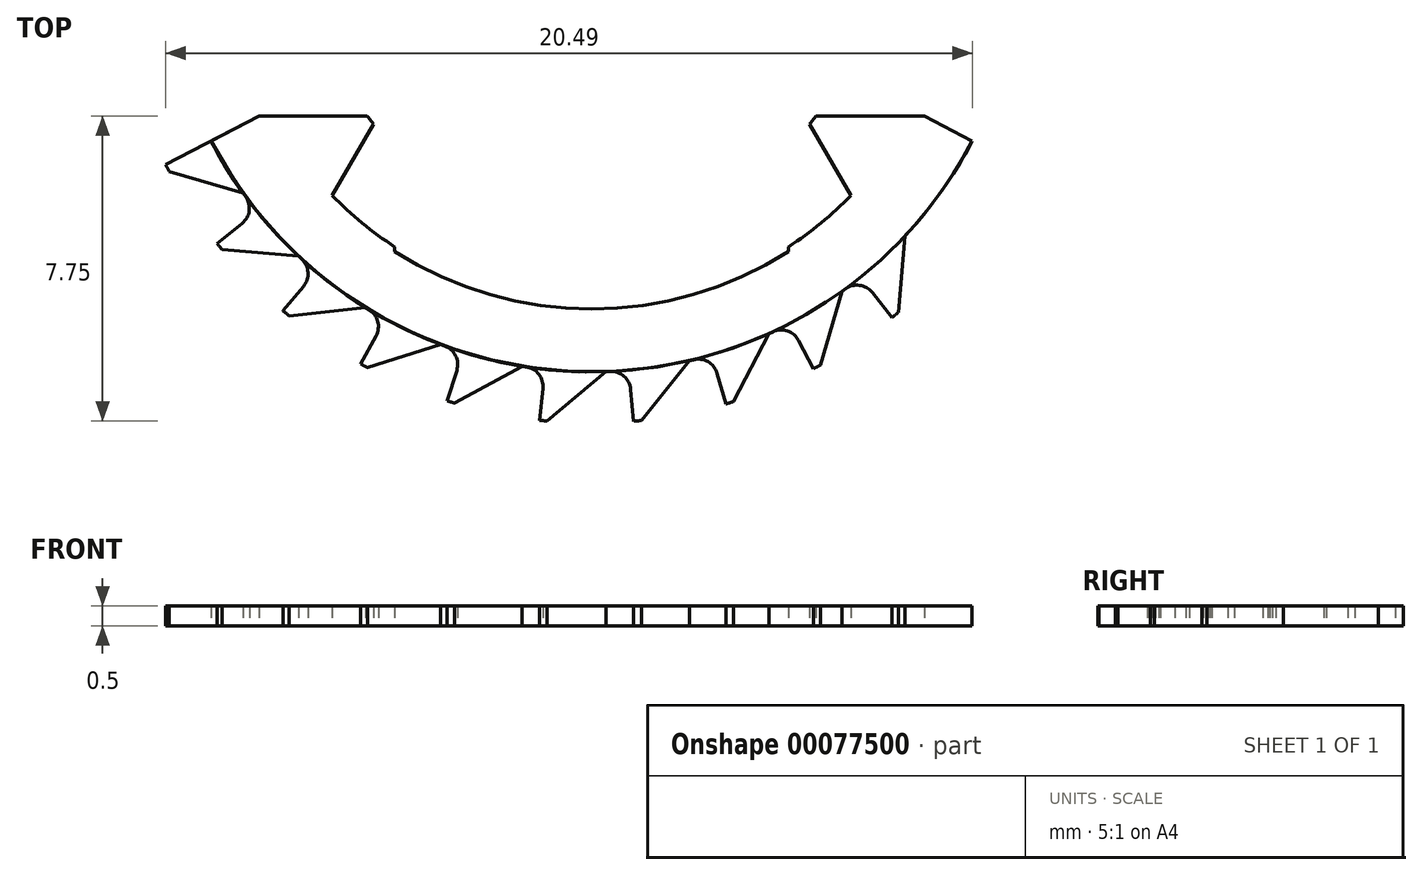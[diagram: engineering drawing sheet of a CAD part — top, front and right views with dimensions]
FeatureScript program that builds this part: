
annotation { "Feature Type Name" : "Feature", "Feature Type Description" : "" }
export const myFeature = defineFeature(function(context is Context, id is Id, definition is map)
    precondition{}
    {
        {
            var Q0;
            Q0=qCreatedBy(makeId("Top.planeOp"),FACE);
            var sketch = newSketch(context, id + "F0", { "sketchPlane" : qUnion([Q0])});
            skArc(sketch, "E0", {"start": v(5, -7.72) * mm, "mid": v(5.83, -7.12) * mm, "end": v(6.6, -6.42) * mm});
            skArc(sketch, "E1", {"start": v(-5, -7.84) * mm, "mid": v(0, -9.3) * mm, "end": v(5, -7.84) * mm});
            skArc(sketch, "E2", {"start": v(7.64, -9.51) * mm, "mid": v(7.71, -9.45) * mm, "end": v(7.8, -9.39) * mm});
            skCircle(sketch, "E3", {"center": v(0, 0) * mm, "radius": 10.9 * mm});
            skLineSegment(sketch, "E4", {"start": v(0, 0) * mm, "end": v(-10.82, -5.63) * mm});
            skLineSegment(sketch, "E5", {"start": v(0, 0) * mm, "end": v(9.67, -5.03) * mm});
            skLineSegment(sketch, "E6", {"start": v(0, 0) * mm, "end": v(7.64, -9.51) * mm, "construction": true});
            skLineSegment(sketch, "E7", {"start": v(6.82, -8.5) * mm, "end": v(7.64, -9.51) * mm});
            skLineSegment(sketch, "E8", {"start": v(7.8, -9.39) * mm, "end": v(7.96, -7.45) * mm});
            skLineSegment(sketch, "E9", {"start": v(0, 0) * mm, "end": v(9.35, -7.84) * mm, "construction": true});
            skLineSegment(sketch, "E10.1.0", {"start": v(5.8, -10.73) * mm, "end": v(6.36, -8.86) * mm});
            skArc(sketch, "E10.1.1", {"start": v(5.63, -10.82) * mm, "mid": v(5.72, -10.77) * mm, "end": v(5.8, -10.73) * mm});
            skLineSegment(sketch, "E10.1.2", {"start": v(5.03, -9.67) * mm, "end": v(5.63, -10.82) * mm});
            skLineSegment(sketch, "E10.2.0", {"start": v(3.6, -11.66) * mm, "end": v(4.5, -9.92) * mm});
            skArc(sketch, "E10.2.1", {"start": v(3.41, -11.71) * mm, "mid": v(3.5, -11.68) * mm, "end": v(3.6, -11.66) * mm});
            skLineSegment(sketch, "E10.2.2", {"start": v(3.05, -10.46) * mm, "end": v(3.41, -11.71) * mm});
            skLineSegment(sketch, "E10.3.0", {"start": v(1.26, -12.13) * mm, "end": v(2.48, -10.61) * mm});
            skArc(sketch, "E10.3.1", {"start": v(1.06, -12.15) * mm, "mid": v(1.16, -12.14) * mm, "end": v(1.26, -12.13) * mm});
            skLineSegment(sketch, "E10.3.2", {"start": v(0.95, -10.86) * mm, "end": v(1.06, -12.15) * mm});
            skLineSegment(sketch, "E10.4.0", {"start": v(-1.13, -12.15) * mm, "end": v(0.36, -10.9) * mm});
            skArc(sketch, "E10.4.1", {"start": v(-1.33, -12.13) * mm, "mid": v(-1.23, -12.14) * mm, "end": v(-1.13, -12.15) * mm});
            skLineSegment(sketch, "E10.4.2", {"start": v(-1.19, -10.84) * mm, "end": v(-1.33, -12.13) * mm});
            skLineSegment(sketch, "E10.5.0", {"start": v(-3.48, -11.7) * mm, "end": v(-1.77, -10.76) * mm});
            skArc(sketch, "E10.5.1", {"start": v(-3.67, -11.64) * mm, "mid": v(-3.57, -11.67) * mm, "end": v(-3.48, -11.7) * mm});
            skLineSegment(sketch, "E10.5.2", {"start": v(-3.28, -10.4) * mm, "end": v(-3.67, -11.64) * mm});
            skLineSegment(sketch, "E10.6.0", {"start": v(-5.7, -10.8) * mm, "end": v(-3.83, -10.2) * mm});
            skArc(sketch, "E10.6.1", {"start": v(-5.87, -10.7) * mm, "mid": v(-5.78, -10.74) * mm, "end": v(-5.7, -10.8) * mm});
            skLineSegment(sketch, "E10.6.2", {"start": v(-5.24, -9.56) * mm, "end": v(-5.87, -10.7) * mm});
            skLineSegment(sketch, "E10.7.0", {"start": v(-7.69, -9.47) * mm, "end": v(-5.75, -9.26) * mm});
            skArc(sketch, "E10.7.1", {"start": v(-7.84, -9.35) * mm, "mid": v(-7.77, -9.4) * mm, "end": v(-7.69, -9.47) * mm});
            skLineSegment(sketch, "E10.7.2", {"start": v(-7, -8.35) * mm, "end": v(-7.84, -9.35) * mm});
            skLineSegment(sketch, "E10.8.0", {"start": v(-9.39, -7.8) * mm, "end": v(-7.45, -7.96) * mm});
            skArc(sketch, "E10.8.1", {"start": v(-9.51, -7.64) * mm, "mid": v(-9.45, -7.71) * mm, "end": v(-9.39, -7.8) * mm});
            skLineSegment(sketch, "E10.8.2", {"start": v(-8.5, -6.82) * mm, "end": v(-9.51, -7.64) * mm});
            skLineSegment(sketch, "E10.9.0", {"start": v(-10.73, -5.8) * mm, "end": v(-8.86, -6.36) * mm});
            skArc(sketch, "E10.9.1", {"start": v(-10.82, -5.63) * mm, "mid": v(-10.77, -5.72) * mm, "end": v(-10.73, -5.8) * mm});
            skLineSegment(sketch, "E10.9.2", {"start": v(-9.67, -5.03) * mm, "end": v(-10.82, -5.63) * mm});
            skLineSegment(sketch, "E10.anchor1", {"start": v(0, 0) * mm, "end": v(7.8, -9.39) * mm, "construction": true});
            skLineSegment(sketch, "E10.anchor2", {"start": v(0, 0) * mm, "end": v(-9.58, -5.2) * mm, "construction": true});
            skArc(sketch, "E11", {"start": v(7.13, -8.88) * mm, "mid": v(6.8, -8.7) * mm, "end": v(6.44, -8.8) * mm});
            skArc(sketch, "E12.1.0", {"start": v(5.26, -10.1) * mm, "mid": v(4.98, -9.86) * mm, "end": v(4.6, -9.88) * mm});
            skArc(sketch, "E12.2.0", {"start": v(3.19, -10.93) * mm, "mid": v(2.96, -10.64) * mm, "end": v(2.59, -10.59) * mm});
            skArc(sketch, "E12.3.0", {"start": v(1, -11.35) * mm, "mid": v(0.82, -11.01) * mm, "end": v(0.47, -10.89) * mm});
            skArc(sketch, "E12.4.0", {"start": v(-1.24, -11.32) * mm, "mid": v(-1.34, -10.96) * mm, "end": v(-1.66, -10.77) * mm});
            skArc(sketch, "E12.5.0", {"start": v(-3.42, -10.86) * mm, "mid": v(-3.45, -10.5) * mm, "end": v(-3.73, -10.24) * mm});
            skArc(sketch, "E12.6.0", {"start": v(-5.48, -9.99) * mm, "mid": v(-5.43, -9.62) * mm, "end": v(-5.66, -9.32) * mm});
            skArc(sketch, "E12.7.0", {"start": v(-7.32, -8.72) * mm, "mid": v(-7.2, -8.37) * mm, "end": v(-7.37, -8.03) * mm});
            skArc(sketch, "E12.8.0", {"start": v(-8.88, -7.13) * mm, "mid": v(-8.7, -6.8) * mm, "end": v(-8.8, -6.44) * mm});
            skLineSegment(sketch, "E12.anchor1", {"start": v(6.44, -8.8) * mm, "end": v(0, 0) * mm, "construction": true});
            skLineSegment(sketch, "E12.anchor2", {"start": v(0, 0) * mm, "end": v(-8.8, -6.44) * mm, "construction": true});
            skCircle(sketch, "E13", {"center": v(0, 0) * mm, "radius": 12.2 * mm, "construction": true});
            skLineSegment(sketch, "E14", {"start": v(-8.45, -4.4) * mm, "end": v(-5.7, -4.4) * mm});
            skPoint(sketch, "E15", {"position": v(0, 5) * mm});
            skLineSegment(sketch, "E16", {"start": v(0, 5) * mm, "end": v(-6.6, -6.42) * mm});
            skLineSegment(sketch, "E17", {"start": v(0, 5) * mm, "end": v(6.6, -6.42) * mm});
            skLineSegment(sketch, "E18", {"start": v(-5, -7.72) * mm, "end": v(-5, -7.84) * mm});
            skLineSegment(sketch, "E19", {"start": v(5, -7.72) * mm, "end": v(5, -7.84) * mm});
            skArc(sketch, "E20.trimOffspring", {"start": v(5.52, -4.63) * mm, "mid": v(5.6, -4.51) * mm, "end": v(5.7, -4.4) * mm});
            skLineSegment(sketch, "E21.trimOffspring", {"start": v(5.7, -4.4) * mm, "end": v(8.45, -4.4) * mm});
            skLineSegment(sketch, "E22.trimOffspring", {"start": v(-9.58, -5.2) * mm, "end": v(-10.73, -5.8) * mm, "construction": true});
            skArc(sketch, "E23", {"start": v(-5.7, -4.4) * mm, "mid": v(-5.62, -4.5) * mm, "end": v(-5.54, -4.6) * mm});
            skArc(sketch, "E24", {"start": v(-6.6, -6.42) * mm, "mid": v(-5.83, -7.12) * mm, "end": v(-5, -7.72) * mm});
            skSolve(sketch);
        }
        {
            var Q0;
            {var subQ6=sQuery(id+"F0.wireOp",EDGE,"E0");Q0=makeQuery(id+"F0.imprint","IMPRINT",FACE,{"disambiguationData":[TD([[makeQuery(id+"F0.imprint","IMPRINT",EDGE,{"derivedFrom":subQ6}),-1.0]])]});}
            var Q1;
            {var subQ1=sQuery(id+"F0.wireOp",EDGE,"E10.9.0");Q1=makeQuery(id+"F0.imprint","IMPRINT",FACE,{"disambiguationData":[TD([[makeQuery(id+"F0.imprint","IMPRINT",EDGE,{"derivedFrom":subQ1}),1.0]])]});}
            var Q2;
            {var subQ5=sQuery(id+"F0.wireOp",EDGE,"E10.8.0");Q2=makeQuery(id+"F0.imprint","IMPRINT",FACE,{"disambiguationData":[TD([[makeQuery(id+"F0.imprint","IMPRINT",EDGE,{"derivedFrom":subQ5}),1.0]])]});}
            var Q3;
            {var subQ5=sQuery(id+"F0.wireOp",EDGE,"E10.7.0");Q3=makeQuery(id+"F0.imprint","IMPRINT",FACE,{"disambiguationData":[TD([[makeQuery(id+"F0.imprint","IMPRINT",EDGE,{"derivedFrom":subQ5}),1.0]])]});}
            var Q4;
            {var subQ5=sQuery(id+"F0.wireOp",EDGE,"E10.6.0");Q4=makeQuery(id+"F0.imprint","IMPRINT",FACE,{"disambiguationData":[TD([[makeQuery(id+"F0.imprint","IMPRINT",EDGE,{"derivedFrom":subQ5}),1.0]])]});}
            var Q5;
            {var subQ5=sQuery(id+"F0.wireOp",EDGE,"E10.5.0");Q5=makeQuery(id+"F0.imprint","IMPRINT",FACE,{"disambiguationData":[TD([[makeQuery(id+"F0.imprint","IMPRINT",EDGE,{"derivedFrom":subQ5}),1.0]])]});}
            var Q6;
            {var subQ5=sQuery(id+"F0.wireOp",EDGE,"E10.4.0");Q6=makeQuery(id+"F0.imprint","IMPRINT",FACE,{"disambiguationData":[TD([[makeQuery(id+"F0.imprint","IMPRINT",EDGE,{"derivedFrom":subQ5}),1.0]])]});}
            var Q7;
            {var subQ5=sQuery(id+"F0.wireOp",EDGE,"E10.3.0");Q7=makeQuery(id+"F0.imprint","IMPRINT",FACE,{"disambiguationData":[TD([[makeQuery(id+"F0.imprint","IMPRINT",EDGE,{"derivedFrom":subQ5}),1.0]])]});}
            var Q8;
            {var subQ2=sQuery(id+"F0.wireOp",EDGE,"E2");Q8=makeQuery(id+"F0.imprint","IMPRINT",FACE,{"disambiguationData":[TD([[makeQuery(id+"F0.imprint","IMPRINT",EDGE,{"derivedFrom":subQ2}),1.0]])]});}
            var Q9;
            {var subQ5=sQuery(id+"F0.wireOp",EDGE,"E10.1.0");Q9=makeQuery(id+"F0.imprint","IMPRINT",FACE,{"disambiguationData":[TD([[makeQuery(id+"F0.imprint","IMPRINT",EDGE,{"derivedFrom":subQ5}),1.0]])]});}
            var Q10;
            {var subQ5=sQuery(id+"F0.wireOp",EDGE,"E10.2.0");Q10=makeQuery(id+"F0.imprint","IMPRINT",FACE,{"disambiguationData":[TD([[makeQuery(id+"F0.imprint","IMPRINT",EDGE,{"derivedFrom":subQ5}),1.0]])]});}
            var Q11;
            {var subQ1=sQuery(id+"F0.wireOp",EDGE,"E11");Q11=makeQuery(id+"F0.imprint","IMPRINT",FACE,{"disambiguationData":[TD([[makeQuery(id+"F0.imprint","IMPRINT",EDGE,{"derivedFrom":subQ1}),-1.0]])]});}
            var Q12;
            {var subQ0=sQuery(id+"F0.wireOp",EDGE,"E12.1.0");Q12=makeQuery(id+"F0.imprint","IMPRINT",FACE,{"disambiguationData":[TD([[makeQuery(id+"F0.imprint","IMPRINT",EDGE,{"derivedFrom":subQ0}),-1.0]])]});}
            var Q13;
            {var subQ0=sQuery(id+"F0.wireOp",EDGE,"E12.2.0");Q13=makeQuery(id+"F0.imprint","IMPRINT",FACE,{"disambiguationData":[TD([[makeQuery(id+"F0.imprint","IMPRINT",EDGE,{"derivedFrom":subQ0}),-1.0]])]});}
            var Q14;
            {var subQ0=sQuery(id+"F0.wireOp",EDGE,"E12.3.0");Q14=makeQuery(id+"F0.imprint","IMPRINT",FACE,{"disambiguationData":[TD([[makeQuery(id+"F0.imprint","IMPRINT",EDGE,{"derivedFrom":subQ0}),-1.0]])]});}
            var Q15;
            {var subQ0=sQuery(id+"F0.wireOp",EDGE,"E12.4.0");Q15=makeQuery(id+"F0.imprint","IMPRINT",FACE,{"disambiguationData":[TD([[makeQuery(id+"F0.imprint","IMPRINT",EDGE,{"derivedFrom":subQ0}),-1.0]])]});}
            var Q16;
            {var subQ0=sQuery(id+"F0.wireOp",EDGE,"E12.5.0");Q16=makeQuery(id+"F0.imprint","IMPRINT",FACE,{"disambiguationData":[TD([[makeQuery(id+"F0.imprint","IMPRINT",EDGE,{"derivedFrom":subQ0}),-1.0]])]});}
            var Q17;
            {var subQ0=sQuery(id+"F0.wireOp",EDGE,"E12.6.0");Q17=makeQuery(id+"F0.imprint","IMPRINT",FACE,{"disambiguationData":[TD([[makeQuery(id+"F0.imprint","IMPRINT",EDGE,{"derivedFrom":subQ0}),-1.0]])]});}
            var Q18;
            {var subQ0=sQuery(id+"F0.wireOp",EDGE,"E12.8.0");Q18=makeQuery(id+"F0.imprint","IMPRINT",FACE,{"disambiguationData":[TD([[makeQuery(id+"F0.imprint","IMPRINT",EDGE,{"derivedFrom":subQ0}),-1.0]])]});}
            var Q19;
            {var subQ0=sQuery(id+"F0.wireOp",EDGE,"E12.7.0");Q19=makeQuery(id+"F0.imprint","IMPRINT",FACE,{"disambiguationData":[TD([[makeQuery(id+"F0.imprint","IMPRINT",EDGE,{"derivedFrom":subQ0}),-1.0]])]});}
            extrude(context, id + "F1", {"entities" : qUnion([Q0, Q1, Q2, Q3, Q4, Q5, Q6, Q7, Q8, Q9, Q10, Q11, Q12, Q13, Q14, Q15, Q16, Q17, Q18, Q19]), "depth" : 0.5 * mm});
        }
        {
            var Q0;
            {var subQ6=sQuery(id+"F0.wireOp",EDGE,"E0");Q0=makeQuery(id+"F0.imprint","IMPRINT",FACE,{"disambiguationData":[TD([[makeQuery(id+"F0.imprint","IMPRINT",EDGE,{"derivedFrom":subQ6}),-1.0]])]});}
            var Q1;
            {var subQ2=sQuery(id+"F0.wireOp",EDGE,"E2");Q1=makeQuery(id+"F0.imprint","IMPRINT",FACE,{"disambiguationData":[TD([[makeQuery(id+"F0.imprint","IMPRINT",EDGE,{"derivedFrom":subQ2}),1.0]])]});}
            var Q2;
            {var subQ1=sQuery(id+"F0.wireOp",EDGE,"E11");Q2=makeQuery(id+"F0.imprint","IMPRINT",FACE,{"disambiguationData":[TD([[makeQuery(id+"F0.imprint","IMPRINT",EDGE,{"derivedFrom":subQ1}),-1.0]])]});}
            var Q3;
            {var subQ5=sQuery(id+"F0.wireOp",EDGE,"E10.1.0");Q3=makeQuery(id+"F0.imprint","IMPRINT",FACE,{"disambiguationData":[TD([[makeQuery(id+"F0.imprint","IMPRINT",EDGE,{"derivedFrom":subQ5}),1.0]])]});}
            var Q4;
            {var subQ0=sQuery(id+"F0.wireOp",EDGE,"E12.1.0");Q4=makeQuery(id+"F0.imprint","IMPRINT",FACE,{"disambiguationData":[TD([[makeQuery(id+"F0.imprint","IMPRINT",EDGE,{"derivedFrom":subQ0}),-1.0]])]});}
            var Q5;
            {var subQ5=sQuery(id+"F0.wireOp",EDGE,"E10.2.0");Q5=makeQuery(id+"F0.imprint","IMPRINT",FACE,{"disambiguationData":[TD([[makeQuery(id+"F0.imprint","IMPRINT",EDGE,{"derivedFrom":subQ5}),1.0]])]});}
            var Q6;
            {var subQ0=sQuery(id+"F0.wireOp",EDGE,"E12.2.0");Q6=makeQuery(id+"F0.imprint","IMPRINT",FACE,{"disambiguationData":[TD([[makeQuery(id+"F0.imprint","IMPRINT",EDGE,{"derivedFrom":subQ0}),-1.0]])]});}
            var Q7;
            {var subQ5=sQuery(id+"F0.wireOp",EDGE,"E10.3.0");Q7=makeQuery(id+"F0.imprint","IMPRINT",FACE,{"disambiguationData":[TD([[makeQuery(id+"F0.imprint","IMPRINT",EDGE,{"derivedFrom":subQ5}),1.0]])]});}
            var Q8;
            {var subQ0=sQuery(id+"F0.wireOp",EDGE,"E12.3.0");Q8=makeQuery(id+"F0.imprint","IMPRINT",FACE,{"disambiguationData":[TD([[makeQuery(id+"F0.imprint","IMPRINT",EDGE,{"derivedFrom":subQ0}),-1.0]])]});}
            var Q9;
            {var subQ5=sQuery(id+"F0.wireOp",EDGE,"E10.4.0");Q9=makeQuery(id+"F0.imprint","IMPRINT",FACE,{"disambiguationData":[TD([[makeQuery(id+"F0.imprint","IMPRINT",EDGE,{"derivedFrom":subQ5}),1.0]])]});}
            var Q10;
            {var subQ0=sQuery(id+"F0.wireOp",EDGE,"E12.4.0");Q10=makeQuery(id+"F0.imprint","IMPRINT",FACE,{"disambiguationData":[TD([[makeQuery(id+"F0.imprint","IMPRINT",EDGE,{"derivedFrom":subQ0}),-1.0]])]});}
            var Q11;
            {var subQ5=sQuery(id+"F0.wireOp",EDGE,"E10.5.0");Q11=makeQuery(id+"F0.imprint","IMPRINT",FACE,{"disambiguationData":[TD([[makeQuery(id+"F0.imprint","IMPRINT",EDGE,{"derivedFrom":subQ5}),1.0]])]});}
            var Q12;
            {var subQ0=sQuery(id+"F0.wireOp",EDGE,"E12.5.0");Q12=makeQuery(id+"F0.imprint","IMPRINT",FACE,{"disambiguationData":[TD([[makeQuery(id+"F0.imprint","IMPRINT",EDGE,{"derivedFrom":subQ0}),-1.0]])]});}
            var Q13;
            {var subQ5=sQuery(id+"F0.wireOp",EDGE,"E10.6.0");Q13=makeQuery(id+"F0.imprint","IMPRINT",FACE,{"disambiguationData":[TD([[makeQuery(id+"F0.imprint","IMPRINT",EDGE,{"derivedFrom":subQ5}),1.0]])]});}
            var Q14;
            {var subQ0=sQuery(id+"F0.wireOp",EDGE,"E12.6.0");Q14=makeQuery(id+"F0.imprint","IMPRINT",FACE,{"disambiguationData":[TD([[makeQuery(id+"F0.imprint","IMPRINT",EDGE,{"derivedFrom":subQ0}),-1.0]])]});}
            var Q15;
            {var subQ5=sQuery(id+"F0.wireOp",EDGE,"E10.7.0");Q15=makeQuery(id+"F0.imprint","IMPRINT",FACE,{"disambiguationData":[TD([[makeQuery(id+"F0.imprint","IMPRINT",EDGE,{"derivedFrom":subQ5}),1.0]])]});}
            var Q16;
            {var subQ0=sQuery(id+"F0.wireOp",EDGE,"E12.7.0");Q16=makeQuery(id+"F0.imprint","IMPRINT",FACE,{"disambiguationData":[TD([[makeQuery(id+"F0.imprint","IMPRINT",EDGE,{"derivedFrom":subQ0}),-1.0]])]});}
            var Q17;
            {var subQ5=sQuery(id+"F0.wireOp",EDGE,"E10.8.0");Q17=makeQuery(id+"F0.imprint","IMPRINT",FACE,{"disambiguationData":[TD([[makeQuery(id+"F0.imprint","IMPRINT",EDGE,{"derivedFrom":subQ5}),1.0]])]});}
            var Q18;
            {var subQ0=sQuery(id+"F0.wireOp",EDGE,"E12.8.0");Q18=makeQuery(id+"F0.imprint","IMPRINT",FACE,{"disambiguationData":[TD([[makeQuery(id+"F0.imprint","IMPRINT",EDGE,{"derivedFrom":subQ0}),-1.0]])]});}
            extrude(context, id + "F2", {"entities" : qUnion([Q0, Q1, Q2, Q3, Q4, Q5, Q6, Q7, Q8, Q9, Q10, Q11, Q12, Q13, Q14, Q15, Q16, Q17, Q18]), "depth" : 0.5 * mm});
        }
        {
            var Q0;
            {var subQ6=sQuery(id+"F0.wireOp",EDGE,"E0");Q0=makeQuery(id+"F0.imprint","IMPRINT",FACE,{"disambiguationData":[TD([[makeQuery(id+"F0.imprint","IMPRINT",EDGE,{"derivedFrom":subQ6}),-1.0]])]});}
            var Q1;
            {var subQ5=sQuery(id+"F0.wireOp",EDGE,"E10.7.0");Q1=makeQuery(id+"F0.imprint","IMPRINT",FACE,{"disambiguationData":[TD([[makeQuery(id+"F0.imprint","IMPRINT",EDGE,{"derivedFrom":subQ5}),1.0]])]});}
            var Q2;
            {var subQ0=sQuery(id+"F0.wireOp",EDGE,"E12.6.0");Q2=makeQuery(id+"F0.imprint","IMPRINT",FACE,{"disambiguationData":[TD([[makeQuery(id+"F0.imprint","IMPRINT",EDGE,{"derivedFrom":subQ0}),-1.0]])]});}
            var Q3;
            {var subQ5=sQuery(id+"F0.wireOp",EDGE,"E10.6.0");Q3=makeQuery(id+"F0.imprint","IMPRINT",FACE,{"disambiguationData":[TD([[makeQuery(id+"F0.imprint","IMPRINT",EDGE,{"derivedFrom":subQ5}),1.0]])]});}
            var Q4;
            {var subQ0=sQuery(id+"F0.wireOp",EDGE,"E12.5.0");Q4=makeQuery(id+"F0.imprint","IMPRINT",FACE,{"disambiguationData":[TD([[makeQuery(id+"F0.imprint","IMPRINT",EDGE,{"derivedFrom":subQ0}),-1.0]])]});}
            var Q5;
            {var subQ5=sQuery(id+"F0.wireOp",EDGE,"E10.5.0");Q5=makeQuery(id+"F0.imprint","IMPRINT",FACE,{"disambiguationData":[TD([[makeQuery(id+"F0.imprint","IMPRINT",EDGE,{"derivedFrom":subQ5}),1.0]])]});}
            var Q6;
            {var subQ0=sQuery(id+"F0.wireOp",EDGE,"E12.4.0");Q6=makeQuery(id+"F0.imprint","IMPRINT",FACE,{"disambiguationData":[TD([[makeQuery(id+"F0.imprint","IMPRINT",EDGE,{"derivedFrom":subQ0}),-1.0]])]});}
            var Q7;
            {var subQ5=sQuery(id+"F0.wireOp",EDGE,"E10.4.0");Q7=makeQuery(id+"F0.imprint","IMPRINT",FACE,{"disambiguationData":[TD([[makeQuery(id+"F0.imprint","IMPRINT",EDGE,{"derivedFrom":subQ5}),1.0]])]});}
            var Q8;
            {var subQ0=sQuery(id+"F0.wireOp",EDGE,"E12.3.0");Q8=makeQuery(id+"F0.imprint","IMPRINT",FACE,{"disambiguationData":[TD([[makeQuery(id+"F0.imprint","IMPRINT",EDGE,{"derivedFrom":subQ0}),-1.0]])]});}
            var Q9;
            {var subQ5=sQuery(id+"F0.wireOp",EDGE,"E10.3.0");Q9=makeQuery(id+"F0.imprint","IMPRINT",FACE,{"disambiguationData":[TD([[makeQuery(id+"F0.imprint","IMPRINT",EDGE,{"derivedFrom":subQ5}),1.0]])]});}
            var Q10;
            {var subQ0=sQuery(id+"F0.wireOp",EDGE,"E12.2.0");Q10=makeQuery(id+"F0.imprint","IMPRINT",FACE,{"disambiguationData":[TD([[makeQuery(id+"F0.imprint","IMPRINT",EDGE,{"derivedFrom":subQ0}),-1.0]])]});}
            var Q11;
            {var subQ5=sQuery(id+"F0.wireOp",EDGE,"E10.2.0");Q11=makeQuery(id+"F0.imprint","IMPRINT",FACE,{"disambiguationData":[TD([[makeQuery(id+"F0.imprint","IMPRINT",EDGE,{"derivedFrom":subQ5}),1.0]])]});}
            var Q12;
            {var subQ0=sQuery(id+"F0.wireOp",EDGE,"E12.1.0");Q12=makeQuery(id+"F0.imprint","IMPRINT",FACE,{"disambiguationData":[TD([[makeQuery(id+"F0.imprint","IMPRINT",EDGE,{"derivedFrom":subQ0}),-1.0]])]});}
            var Q13;
            {var subQ5=sQuery(id+"F0.wireOp",EDGE,"E10.1.0");Q13=makeQuery(id+"F0.imprint","IMPRINT",FACE,{"disambiguationData":[TD([[makeQuery(id+"F0.imprint","IMPRINT",EDGE,{"derivedFrom":subQ5}),1.0]])]});}
            var Q14;
            {var subQ2=sQuery(id+"F0.wireOp",EDGE,"E2");Q14=makeQuery(id+"F0.imprint","IMPRINT",FACE,{"disambiguationData":[TD([[makeQuery(id+"F0.imprint","IMPRINT",EDGE,{"derivedFrom":subQ2}),1.0]])]});}
            var Q15;
            {var subQ1=sQuery(id+"F0.wireOp",EDGE,"E11");Q15=makeQuery(id+"F0.imprint","IMPRINT",FACE,{"disambiguationData":[TD([[makeQuery(id+"F0.imprint","IMPRINT",EDGE,{"derivedFrom":subQ1}),-1.0]])]});}
            var Q16;
            {var subQ0=sQuery(id+"F0.wireOp",EDGE,"E12.7.0");Q16=makeQuery(id+"F0.imprint","IMPRINT",FACE,{"disambiguationData":[TD([[makeQuery(id+"F0.imprint","IMPRINT",EDGE,{"derivedFrom":subQ0}),-1.0]])]});}
            extrude(context, id + "F3", {"entities" : qUnion([Q0, Q1, Q2, Q3, Q4, Q5, Q6, Q7, Q8, Q9, Q10, Q11, Q12, Q13, Q14, Q15, Q16]), "depth" : 0.5 * mm});
        }
        {
            var Q0;
            {var subQ2=sQuery(id+"F0.wireOp",EDGE,"E2");Q0=makeQuery(id+"F0.imprint","IMPRINT",FACE,{"disambiguationData":[TD([[makeQuery(id+"F0.imprint","IMPRINT",EDGE,{"derivedFrom":subQ2}),1.0]])]});}
            var Q1;
            {var subQ1=sQuery(id+"F0.wireOp",EDGE,"E11");Q1=makeQuery(id+"F0.imprint","IMPRINT",FACE,{"disambiguationData":[TD([[makeQuery(id+"F0.imprint","IMPRINT",EDGE,{"derivedFrom":subQ1}),-1.0]])]});}
            var Q2;
            {var subQ5=sQuery(id+"F0.wireOp",EDGE,"E10.1.0");Q2=makeQuery(id+"F0.imprint","IMPRINT",FACE,{"disambiguationData":[TD([[makeQuery(id+"F0.imprint","IMPRINT",EDGE,{"derivedFrom":subQ5}),1.0]])]});}
            var Q3;
            {var subQ0=sQuery(id+"F0.wireOp",EDGE,"E12.1.0");Q3=makeQuery(id+"F0.imprint","IMPRINT",FACE,{"disambiguationData":[TD([[makeQuery(id+"F0.imprint","IMPRINT",EDGE,{"derivedFrom":subQ0}),-1.0]])]});}
            var Q4;
            {var subQ5=sQuery(id+"F0.wireOp",EDGE,"E10.2.0");Q4=makeQuery(id+"F0.imprint","IMPRINT",FACE,{"disambiguationData":[TD([[makeQuery(id+"F0.imprint","IMPRINT",EDGE,{"derivedFrom":subQ5}),1.0]])]});}
            var Q5;
            {var subQ0=sQuery(id+"F0.wireOp",EDGE,"E12.2.0");Q5=makeQuery(id+"F0.imprint","IMPRINT",FACE,{"disambiguationData":[TD([[makeQuery(id+"F0.imprint","IMPRINT",EDGE,{"derivedFrom":subQ0}),-1.0]])]});}
            var Q6;
            {var subQ5=sQuery(id+"F0.wireOp",EDGE,"E10.3.0");Q6=makeQuery(id+"F0.imprint","IMPRINT",FACE,{"disambiguationData":[TD([[makeQuery(id+"F0.imprint","IMPRINT",EDGE,{"derivedFrom":subQ5}),1.0]])]});}
            var Q7;
            {var subQ0=sQuery(id+"F0.wireOp",EDGE,"E12.3.0");Q7=makeQuery(id+"F0.imprint","IMPRINT",FACE,{"disambiguationData":[TD([[makeQuery(id+"F0.imprint","IMPRINT",EDGE,{"derivedFrom":subQ0}),-1.0]])]});}
            var Q8;
            {var subQ5=sQuery(id+"F0.wireOp",EDGE,"E10.4.0");Q8=makeQuery(id+"F0.imprint","IMPRINT",FACE,{"disambiguationData":[TD([[makeQuery(id+"F0.imprint","IMPRINT",EDGE,{"derivedFrom":subQ5}),1.0]])]});}
            var Q9;
            {var subQ0=sQuery(id+"F0.wireOp",EDGE,"E12.4.0");Q9=makeQuery(id+"F0.imprint","IMPRINT",FACE,{"disambiguationData":[TD([[makeQuery(id+"F0.imprint","IMPRINT",EDGE,{"derivedFrom":subQ0}),-1.0]])]});}
            var Q10;
            {var subQ5=sQuery(id+"F0.wireOp",EDGE,"E10.5.0");Q10=makeQuery(id+"F0.imprint","IMPRINT",FACE,{"disambiguationData":[TD([[makeQuery(id+"F0.imprint","IMPRINT",EDGE,{"derivedFrom":subQ5}),1.0]])]});}
            var Q11;
            {var subQ0=sQuery(id+"F0.wireOp",EDGE,"E12.5.0");Q11=makeQuery(id+"F0.imprint","IMPRINT",FACE,{"disambiguationData":[TD([[makeQuery(id+"F0.imprint","IMPRINT",EDGE,{"derivedFrom":subQ0}),-1.0]])]});}
            var Q12;
            {var subQ5=sQuery(id+"F0.wireOp",EDGE,"E10.6.0");Q12=makeQuery(id+"F0.imprint","IMPRINT",FACE,{"disambiguationData":[TD([[makeQuery(id+"F0.imprint","IMPRINT",EDGE,{"derivedFrom":subQ5}),1.0]])]});}
            var Q13;
            {var subQ6=sQuery(id+"F0.wireOp",EDGE,"E0");Q13=makeQuery(id+"F0.imprint","IMPRINT",FACE,{"disambiguationData":[TD([[makeQuery(id+"F0.imprint","IMPRINT",EDGE,{"derivedFrom":subQ6}),-1.0]])]});}
            var Q14;
            {var subQ0=sQuery(id+"F0.wireOp",EDGE,"E12.6.0");Q14=makeQuery(id+"F0.imprint","IMPRINT",FACE,{"disambiguationData":[TD([[makeQuery(id+"F0.imprint","IMPRINT",EDGE,{"derivedFrom":subQ0}),-1.0]])]});}
            extrude(context, id + "F4", {"entities" : qUnion([Q0, Q1, Q2, Q3, Q4, Q5, Q6, Q7, Q8, Q9, Q10, Q11, Q12, Q13, Q14]), "depth" : 0.5 * mm});
        }
        {
            var Q0;
            {var subQ6=sQuery(id+"F0.wireOp",EDGE,"E0");Q0=makeQuery(id+"F0.imprint","IMPRINT",FACE,{"disambiguationData":[TD([[makeQuery(id+"F0.imprint","IMPRINT",EDGE,{"derivedFrom":subQ6}),-1.0]])]});}
            var Q1;
            {var subQ5=sQuery(id+"F0.wireOp",EDGE,"E10.5.0");Q1=makeQuery(id+"F0.imprint","IMPRINT",FACE,{"disambiguationData":[TD([[makeQuery(id+"F0.imprint","IMPRINT",EDGE,{"derivedFrom":subQ5}),1.0]])]});}
            var Q2;
            {var subQ0=sQuery(id+"F0.wireOp",EDGE,"E12.4.0");Q2=makeQuery(id+"F0.imprint","IMPRINT",FACE,{"disambiguationData":[TD([[makeQuery(id+"F0.imprint","IMPRINT",EDGE,{"derivedFrom":subQ0}),-1.0]])]});}
            var Q3;
            {var subQ5=sQuery(id+"F0.wireOp",EDGE,"E10.4.0");Q3=makeQuery(id+"F0.imprint","IMPRINT",FACE,{"disambiguationData":[TD([[makeQuery(id+"F0.imprint","IMPRINT",EDGE,{"derivedFrom":subQ5}),1.0]])]});}
            var Q4;
            {var subQ0=sQuery(id+"F0.wireOp",EDGE,"E12.3.0");Q4=makeQuery(id+"F0.imprint","IMPRINT",FACE,{"disambiguationData":[TD([[makeQuery(id+"F0.imprint","IMPRINT",EDGE,{"derivedFrom":subQ0}),-1.0]])]});}
            var Q5;
            {var subQ5=sQuery(id+"F0.wireOp",EDGE,"E10.3.0");Q5=makeQuery(id+"F0.imprint","IMPRINT",FACE,{"disambiguationData":[TD([[makeQuery(id+"F0.imprint","IMPRINT",EDGE,{"derivedFrom":subQ5}),1.0]])]});}
            var Q6;
            {var subQ0=sQuery(id+"F0.wireOp",EDGE,"E12.2.0");Q6=makeQuery(id+"F0.imprint","IMPRINT",FACE,{"disambiguationData":[TD([[makeQuery(id+"F0.imprint","IMPRINT",EDGE,{"derivedFrom":subQ0}),-1.0]])]});}
            var Q7;
            {var subQ5=sQuery(id+"F0.wireOp",EDGE,"E10.2.0");Q7=makeQuery(id+"F0.imprint","IMPRINT",FACE,{"disambiguationData":[TD([[makeQuery(id+"F0.imprint","IMPRINT",EDGE,{"derivedFrom":subQ5}),1.0]])]});}
            var Q8;
            {var subQ0=sQuery(id+"F0.wireOp",EDGE,"E12.1.0");Q8=makeQuery(id+"F0.imprint","IMPRINT",FACE,{"disambiguationData":[TD([[makeQuery(id+"F0.imprint","IMPRINT",EDGE,{"derivedFrom":subQ0}),-1.0]])]});}
            var Q9;
            {var subQ5=sQuery(id+"F0.wireOp",EDGE,"E10.1.0");Q9=makeQuery(id+"F0.imprint","IMPRINT",FACE,{"disambiguationData":[TD([[makeQuery(id+"F0.imprint","IMPRINT",EDGE,{"derivedFrom":subQ5}),1.0]])]});}
            var Q10;
            {var subQ1=sQuery(id+"F0.wireOp",EDGE,"E11");Q10=makeQuery(id+"F0.imprint","IMPRINT",FACE,{"disambiguationData":[TD([[makeQuery(id+"F0.imprint","IMPRINT",EDGE,{"derivedFrom":subQ1}),-1.0]])]});}
            var Q11;
            {var subQ2=sQuery(id+"F0.wireOp",EDGE,"E2");Q11=makeQuery(id+"F0.imprint","IMPRINT",FACE,{"disambiguationData":[TD([[makeQuery(id+"F0.imprint","IMPRINT",EDGE,{"derivedFrom":subQ2}),1.0]])]});}
            var Q12;
            {var subQ0=sQuery(id+"F0.wireOp",EDGE,"E12.5.0");Q12=makeQuery(id+"F0.imprint","IMPRINT",FACE,{"disambiguationData":[TD([[makeQuery(id+"F0.imprint","IMPRINT",EDGE,{"derivedFrom":subQ0}),-1.0]])]});}
            extrude(context, id + "F5", {"entities" : qUnion([Q0, Q1, Q2, Q3, Q4, Q5, Q6, Q7, Q8, Q9, Q10, Q11, Q12]), "depth" : 0.5 * mm});
        }
        {
            var Q0;
            {var subQ5=sQuery(id+"F0.wireOp",EDGE,"E10.4.0");Q0=makeQuery(id+"F0.imprint","IMPRINT",FACE,{"disambiguationData":[TD([[makeQuery(id+"F0.imprint","IMPRINT",EDGE,{"derivedFrom":subQ5}),1.0]])]});}
            var Q1;
            {var subQ6=sQuery(id+"F0.wireOp",EDGE,"E0");Q1=makeQuery(id+"F0.imprint","IMPRINT",FACE,{"disambiguationData":[TD([[makeQuery(id+"F0.imprint","IMPRINT",EDGE,{"derivedFrom":subQ6}),-1.0]])]});}
            var Q2;
            {var subQ0=sQuery(id+"F0.wireOp",EDGE,"E12.3.0");Q2=makeQuery(id+"F0.imprint","IMPRINT",FACE,{"disambiguationData":[TD([[makeQuery(id+"F0.imprint","IMPRINT",EDGE,{"derivedFrom":subQ0}),-1.0]])]});}
            var Q3;
            {var subQ5=sQuery(id+"F0.wireOp",EDGE,"E10.3.0");Q3=makeQuery(id+"F0.imprint","IMPRINT",FACE,{"disambiguationData":[TD([[makeQuery(id+"F0.imprint","IMPRINT",EDGE,{"derivedFrom":subQ5}),1.0]])]});}
            var Q4;
            {var subQ0=sQuery(id+"F0.wireOp",EDGE,"E12.2.0");Q4=makeQuery(id+"F0.imprint","IMPRINT",FACE,{"disambiguationData":[TD([[makeQuery(id+"F0.imprint","IMPRINT",EDGE,{"derivedFrom":subQ0}),-1.0]])]});}
            var Q5;
            {var subQ5=sQuery(id+"F0.wireOp",EDGE,"E10.2.0");Q5=makeQuery(id+"F0.imprint","IMPRINT",FACE,{"disambiguationData":[TD([[makeQuery(id+"F0.imprint","IMPRINT",EDGE,{"derivedFrom":subQ5}),1.0]])]});}
            var Q6;
            {var subQ0=sQuery(id+"F0.wireOp",EDGE,"E12.1.0");Q6=makeQuery(id+"F0.imprint","IMPRINT",FACE,{"disambiguationData":[TD([[makeQuery(id+"F0.imprint","IMPRINT",EDGE,{"derivedFrom":subQ0}),-1.0]])]});}
            var Q7;
            {var subQ5=sQuery(id+"F0.wireOp",EDGE,"E10.1.0");Q7=makeQuery(id+"F0.imprint","IMPRINT",FACE,{"disambiguationData":[TD([[makeQuery(id+"F0.imprint","IMPRINT",EDGE,{"derivedFrom":subQ5}),1.0]])]});}
            var Q8;
            {var subQ1=sQuery(id+"F0.wireOp",EDGE,"E11");Q8=makeQuery(id+"F0.imprint","IMPRINT",FACE,{"disambiguationData":[TD([[makeQuery(id+"F0.imprint","IMPRINT",EDGE,{"derivedFrom":subQ1}),-1.0]])]});}
            var Q9;
            {var subQ2=sQuery(id+"F0.wireOp",EDGE,"E2");Q9=makeQuery(id+"F0.imprint","IMPRINT",FACE,{"disambiguationData":[TD([[makeQuery(id+"F0.imprint","IMPRINT",EDGE,{"derivedFrom":subQ2}),1.0]])]});}
            var Q10;
            {var subQ0=sQuery(id+"F0.wireOp",EDGE,"E12.4.0");Q10=makeQuery(id+"F0.imprint","IMPRINT",FACE,{"disambiguationData":[TD([[makeQuery(id+"F0.imprint","IMPRINT",EDGE,{"derivedFrom":subQ0}),-1.0]])]});}
            extrude(context, id + "F6", {"entities" : qUnion([Q0, Q1, Q2, Q3, Q4, Q5, Q6, Q7, Q8, Q9, Q10]), "depth" : 0.5 * mm});
        }
        {
            var Q0;
            {var subQ6=sQuery(id+"F0.wireOp",EDGE,"E0");Q0=makeQuery(id+"F0.imprint","IMPRINT",FACE,{"disambiguationData":[TD([[makeQuery(id+"F0.imprint","IMPRINT",EDGE,{"derivedFrom":subQ6}),-1.0]])]});}
            var Q1;
            {var subQ5=sQuery(id+"F0.wireOp",EDGE,"E10.3.0");Q1=makeQuery(id+"F0.imprint","IMPRINT",FACE,{"disambiguationData":[TD([[makeQuery(id+"F0.imprint","IMPRINT",EDGE,{"derivedFrom":subQ5}),1.0]])]});}
            var Q2;
            {var subQ0=sQuery(id+"F0.wireOp",EDGE,"E12.2.0");Q2=makeQuery(id+"F0.imprint","IMPRINT",FACE,{"disambiguationData":[TD([[makeQuery(id+"F0.imprint","IMPRINT",EDGE,{"derivedFrom":subQ0}),-1.0]])]});}
            var Q3;
            {var subQ5=sQuery(id+"F0.wireOp",EDGE,"E10.2.0");Q3=makeQuery(id+"F0.imprint","IMPRINT",FACE,{"disambiguationData":[TD([[makeQuery(id+"F0.imprint","IMPRINT",EDGE,{"derivedFrom":subQ5}),1.0]])]});}
            var Q4;
            {var subQ0=sQuery(id+"F0.wireOp",EDGE,"E12.1.0");Q4=makeQuery(id+"F0.imprint","IMPRINT",FACE,{"disambiguationData":[TD([[makeQuery(id+"F0.imprint","IMPRINT",EDGE,{"derivedFrom":subQ0}),-1.0]])]});}
            var Q5;
            {var subQ5=sQuery(id+"F0.wireOp",EDGE,"E10.1.0");Q5=makeQuery(id+"F0.imprint","IMPRINT",FACE,{"disambiguationData":[TD([[makeQuery(id+"F0.imprint","IMPRINT",EDGE,{"derivedFrom":subQ5}),1.0]])]});}
            var Q6;
            {var subQ1=sQuery(id+"F0.wireOp",EDGE,"E11");Q6=makeQuery(id+"F0.imprint","IMPRINT",FACE,{"disambiguationData":[TD([[makeQuery(id+"F0.imprint","IMPRINT",EDGE,{"derivedFrom":subQ1}),-1.0]])]});}
            var Q7;
            {var subQ2=sQuery(id+"F0.wireOp",EDGE,"E2");Q7=makeQuery(id+"F0.imprint","IMPRINT",FACE,{"disambiguationData":[TD([[makeQuery(id+"F0.imprint","IMPRINT",EDGE,{"derivedFrom":subQ2}),1.0]])]});}
            var Q8;
            {var subQ0=sQuery(id+"F0.wireOp",EDGE,"E12.3.0");Q8=makeQuery(id+"F0.imprint","IMPRINT",FACE,{"disambiguationData":[TD([[makeQuery(id+"F0.imprint","IMPRINT",EDGE,{"derivedFrom":subQ0}),-1.0]])]});}
            extrude(context, id + "F7", {"entities" : qUnion([Q0, Q1, Q2, Q3, Q4, Q5, Q6, Q7, Q8]), "depth" : 0.5 * mm});
        }
        {
            var Q0;
            {var subQ6=sQuery(id+"F0.wireOp",EDGE,"E0");Q0=makeQuery(id+"F0.imprint","IMPRINT",FACE,{"disambiguationData":[TD([[makeQuery(id+"F0.imprint","IMPRINT",EDGE,{"derivedFrom":subQ6}),-1.0]])]});}
            var Q1;
            {var subQ5=sQuery(id+"F0.wireOp",EDGE,"E10.2.0");Q1=makeQuery(id+"F0.imprint","IMPRINT",FACE,{"disambiguationData":[TD([[makeQuery(id+"F0.imprint","IMPRINT",EDGE,{"derivedFrom":subQ5}),1.0]])]});}
            var Q2;
            {var subQ0=sQuery(id+"F0.wireOp",EDGE,"E12.1.0");Q2=makeQuery(id+"F0.imprint","IMPRINT",FACE,{"disambiguationData":[TD([[makeQuery(id+"F0.imprint","IMPRINT",EDGE,{"derivedFrom":subQ0}),-1.0]])]});}
            var Q3;
            {var subQ5=sQuery(id+"F0.wireOp",EDGE,"E10.1.0");Q3=makeQuery(id+"F0.imprint","IMPRINT",FACE,{"disambiguationData":[TD([[makeQuery(id+"F0.imprint","IMPRINT",EDGE,{"derivedFrom":subQ5}),1.0]])]});}
            var Q4;
            {var subQ1=sQuery(id+"F0.wireOp",EDGE,"E11");Q4=makeQuery(id+"F0.imprint","IMPRINT",FACE,{"disambiguationData":[TD([[makeQuery(id+"F0.imprint","IMPRINT",EDGE,{"derivedFrom":subQ1}),-1.0]])]});}
            var Q5;
            {var subQ2=sQuery(id+"F0.wireOp",EDGE,"E2");Q5=makeQuery(id+"F0.imprint","IMPRINT",FACE,{"disambiguationData":[TD([[makeQuery(id+"F0.imprint","IMPRINT",EDGE,{"derivedFrom":subQ2}),1.0]])]});}
            var Q6;
            {var subQ0=sQuery(id+"F0.wireOp",EDGE,"E12.2.0");Q6=makeQuery(id+"F0.imprint","IMPRINT",FACE,{"disambiguationData":[TD([[makeQuery(id+"F0.imprint","IMPRINT",EDGE,{"derivedFrom":subQ0}),-1.0]])]});}
            extrude(context, id + "F8", {"entities" : qUnion([Q0, Q1, Q2, Q3, Q4, Q5, Q6]), "depth" : 0.5 * mm});
        }
        {
            var Q0;
            {var subQ6=sQuery(id+"F0.wireOp",EDGE,"E0");Q0=makeQuery(id+"F0.imprint","IMPRINT",FACE,{"disambiguationData":[TD([[makeQuery(id+"F0.imprint","IMPRINT",EDGE,{"derivedFrom":subQ6}),-1.0]])]});}
            var Q1;
            {var subQ5=sQuery(id+"F0.wireOp",EDGE,"E10.1.0");Q1=makeQuery(id+"F0.imprint","IMPRINT",FACE,{"disambiguationData":[TD([[makeQuery(id+"F0.imprint","IMPRINT",EDGE,{"derivedFrom":subQ5}),1.0]])]});}
            var Q2;
            {var subQ1=sQuery(id+"F0.wireOp",EDGE,"E11");Q2=makeQuery(id+"F0.imprint","IMPRINT",FACE,{"disambiguationData":[TD([[makeQuery(id+"F0.imprint","IMPRINT",EDGE,{"derivedFrom":subQ1}),-1.0]])]});}
            var Q3;
            {var subQ2=sQuery(id+"F0.wireOp",EDGE,"E2");Q3=makeQuery(id+"F0.imprint","IMPRINT",FACE,{"disambiguationData":[TD([[makeQuery(id+"F0.imprint","IMPRINT",EDGE,{"derivedFrom":subQ2}),1.0]])]});}
            var Q4;
            {var subQ0=sQuery(id+"F0.wireOp",EDGE,"E12.1.0");Q4=makeQuery(id+"F0.imprint","IMPRINT",FACE,{"disambiguationData":[TD([[makeQuery(id+"F0.imprint","IMPRINT",EDGE,{"derivedFrom":subQ0}),-1.0]])]});}
            extrude(context, id + "F9", {"entities" : qUnion([Q0, Q1, Q2, Q3, Q4]), "depth" : 0.5 * mm});
        }
        {
            var Q0;
            {var subQ6=sQuery(id+"F0.wireOp",EDGE,"E0");Q0=makeQuery(id+"F0.imprint","IMPRINT",FACE,{"disambiguationData":[TD([[makeQuery(id+"F0.imprint","IMPRINT",EDGE,{"derivedFrom":subQ6}),-1.0]])]});}
            var Q1;
            {var subQ2=sQuery(id+"F0.wireOp",EDGE,"E2");Q1=makeQuery(id+"F0.imprint","IMPRINT",FACE,{"disambiguationData":[TD([[makeQuery(id+"F0.imprint","IMPRINT",EDGE,{"derivedFrom":subQ2}),1.0]])]});}
            var Q2;
            {var subQ1=sQuery(id+"F0.wireOp",EDGE,"E11");Q2=makeQuery(id+"F0.imprint","IMPRINT",FACE,{"disambiguationData":[TD([[makeQuery(id+"F0.imprint","IMPRINT",EDGE,{"derivedFrom":subQ1}),-1.0]])]});}
            extrude(context, id + "F10", {"entities" : qUnion([Q0, Q1, Q2]), "depth" : 0.5 * mm});
        }
        {
            var Q0;
            {var subQ5=sQuery(id+"F0.wireOp",EDGE,"E10.1.0");Q0=makeQuery(id+"F0.imprint","IMPRINT",FACE,{"disambiguationData":[TD([[makeQuery(id+"F0.imprint","IMPRINT",EDGE,{"derivedFrom":subQ5}),1.0]])]});}
            var Q1;
            {var subQ0=sQuery(id+"F0.wireOp",EDGE,"E12.1.0");Q1=makeQuery(id+"F0.imprint","IMPRINT",FACE,{"disambiguationData":[TD([[makeQuery(id+"F0.imprint","IMPRINT",EDGE,{"derivedFrom":subQ0}),-1.0]])]});}
            var Q2;
            {var subQ6=sQuery(id+"F0.wireOp",EDGE,"E0");Q2=makeQuery(id+"F0.imprint","IMPRINT",FACE,{"disambiguationData":[TD([[makeQuery(id+"F0.imprint","IMPRINT",EDGE,{"derivedFrom":subQ6}),-1.0]])]});}
            extrude(context, id + "F11", {"entities" : qUnion([Q0, Q1, Q2]), "depth" : 0.5 * mm});
        }
        {
            var Q0;
            {var subQ5=sQuery(id+"F0.wireOp",EDGE,"E10.1.0");Q0=makeQuery(id+"F0.imprint","IMPRINT",FACE,{"disambiguationData":[TD([[makeQuery(id+"F0.imprint","IMPRINT",EDGE,{"derivedFrom":subQ5}),1.0]])]});}
            var Q1;
            {var subQ6=sQuery(id+"F0.wireOp",EDGE,"E0");Q1=makeQuery(id+"F0.imprint","IMPRINT",FACE,{"disambiguationData":[TD([[makeQuery(id+"F0.imprint","IMPRINT",EDGE,{"derivedFrom":subQ6}),-1.0]])]});}
            var Q2;
            {var subQ5=sQuery(id+"F0.wireOp",EDGE,"E10.2.0");Q2=makeQuery(id+"F0.imprint","IMPRINT",FACE,{"disambiguationData":[TD([[makeQuery(id+"F0.imprint","IMPRINT",EDGE,{"derivedFrom":subQ5}),1.0]])]});}
            var Q3;
            {var subQ5=sQuery(id+"F0.wireOp",EDGE,"E10.3.0");Q3=makeQuery(id+"F0.imprint","IMPRINT",FACE,{"disambiguationData":[TD([[makeQuery(id+"F0.imprint","IMPRINT",EDGE,{"derivedFrom":subQ5}),1.0]])]});}
            var Q4;
            {var subQ5=sQuery(id+"F0.wireOp",EDGE,"E10.4.0");Q4=makeQuery(id+"F0.imprint","IMPRINT",FACE,{"disambiguationData":[TD([[makeQuery(id+"F0.imprint","IMPRINT",EDGE,{"derivedFrom":subQ5}),1.0]])]});}
            var Q5;
            {var subQ5=sQuery(id+"F0.wireOp",EDGE,"E10.5.0");Q5=makeQuery(id+"F0.imprint","IMPRINT",FACE,{"disambiguationData":[TD([[makeQuery(id+"F0.imprint","IMPRINT",EDGE,{"derivedFrom":subQ5}),1.0]])]});}
            var Q6;
            {var subQ5=sQuery(id+"F0.wireOp",EDGE,"E10.6.0");Q6=makeQuery(id+"F0.imprint","IMPRINT",FACE,{"disambiguationData":[TD([[makeQuery(id+"F0.imprint","IMPRINT",EDGE,{"derivedFrom":subQ5}),1.0]])]});}
            var Q7;
            {var subQ5=sQuery(id+"F0.wireOp",EDGE,"E10.7.0");Q7=makeQuery(id+"F0.imprint","IMPRINT",FACE,{"disambiguationData":[TD([[makeQuery(id+"F0.imprint","IMPRINT",EDGE,{"derivedFrom":subQ5}),1.0]])]});}
            var Q8;
            {var subQ5=sQuery(id+"F0.wireOp",EDGE,"E10.8.0");Q8=makeQuery(id+"F0.imprint","IMPRINT",FACE,{"disambiguationData":[TD([[makeQuery(id+"F0.imprint","IMPRINT",EDGE,{"derivedFrom":subQ5}),1.0]])]});}
            var Q9;
            {var subQ1=sQuery(id+"F0.wireOp",EDGE,"E10.9.0");Q9=makeQuery(id+"F0.imprint","IMPRINT",FACE,{"disambiguationData":[TD([[makeQuery(id+"F0.imprint","IMPRINT",EDGE,{"derivedFrom":subQ1}),1.0]])]});}
            var Q10;
            {var subQ0=sQuery(id+"F0.wireOp",EDGE,"E12.8.0");Q10=makeQuery(id+"F0.imprint","IMPRINT",FACE,{"disambiguationData":[TD([[makeQuery(id+"F0.imprint","IMPRINT",EDGE,{"derivedFrom":subQ0}),-1.0]])]});}
            var Q11;
            {var subQ0=sQuery(id+"F0.wireOp",EDGE,"E12.7.0");Q11=makeQuery(id+"F0.imprint","IMPRINT",FACE,{"disambiguationData":[TD([[makeQuery(id+"F0.imprint","IMPRINT",EDGE,{"derivedFrom":subQ0}),-1.0]])]});}
            var Q12;
            {var subQ0=sQuery(id+"F0.wireOp",EDGE,"E12.6.0");Q12=makeQuery(id+"F0.imprint","IMPRINT",FACE,{"disambiguationData":[TD([[makeQuery(id+"F0.imprint","IMPRINT",EDGE,{"derivedFrom":subQ0}),-1.0]])]});}
            var Q13;
            {var subQ0=sQuery(id+"F0.wireOp",EDGE,"E12.5.0");Q13=makeQuery(id+"F0.imprint","IMPRINT",FACE,{"disambiguationData":[TD([[makeQuery(id+"F0.imprint","IMPRINT",EDGE,{"derivedFrom":subQ0}),-1.0]])]});}
            var Q14;
            {var subQ0=sQuery(id+"F0.wireOp",EDGE,"E12.4.0");Q14=makeQuery(id+"F0.imprint","IMPRINT",FACE,{"disambiguationData":[TD([[makeQuery(id+"F0.imprint","IMPRINT",EDGE,{"derivedFrom":subQ0}),-1.0]])]});}
            var Q15;
            {var subQ0=sQuery(id+"F0.wireOp",EDGE,"E12.3.0");Q15=makeQuery(id+"F0.imprint","IMPRINT",FACE,{"disambiguationData":[TD([[makeQuery(id+"F0.imprint","IMPRINT",EDGE,{"derivedFrom":subQ0}),-1.0]])]});}
            var Q16;
            {var subQ0=sQuery(id+"F0.wireOp",EDGE,"E12.2.0");Q16=makeQuery(id+"F0.imprint","IMPRINT",FACE,{"disambiguationData":[TD([[makeQuery(id+"F0.imprint","IMPRINT",EDGE,{"derivedFrom":subQ0}),-1.0]])]});}
            var Q17;
            {var subQ0=sQuery(id+"F0.wireOp",EDGE,"E12.1.0");Q17=makeQuery(id+"F0.imprint","IMPRINT",FACE,{"disambiguationData":[TD([[makeQuery(id+"F0.imprint","IMPRINT",EDGE,{"derivedFrom":subQ0}),-1.0]])]});}
            extrude(context, id + "F12", {"entities" : qUnion([Q0, Q1, Q2, Q3, Q4, Q5, Q6, Q7, Q8, Q9, Q10, Q11, Q12, Q13, Q14, Q15, Q16, Q17]), "depth" : 0.5 * mm});
        }
    });
